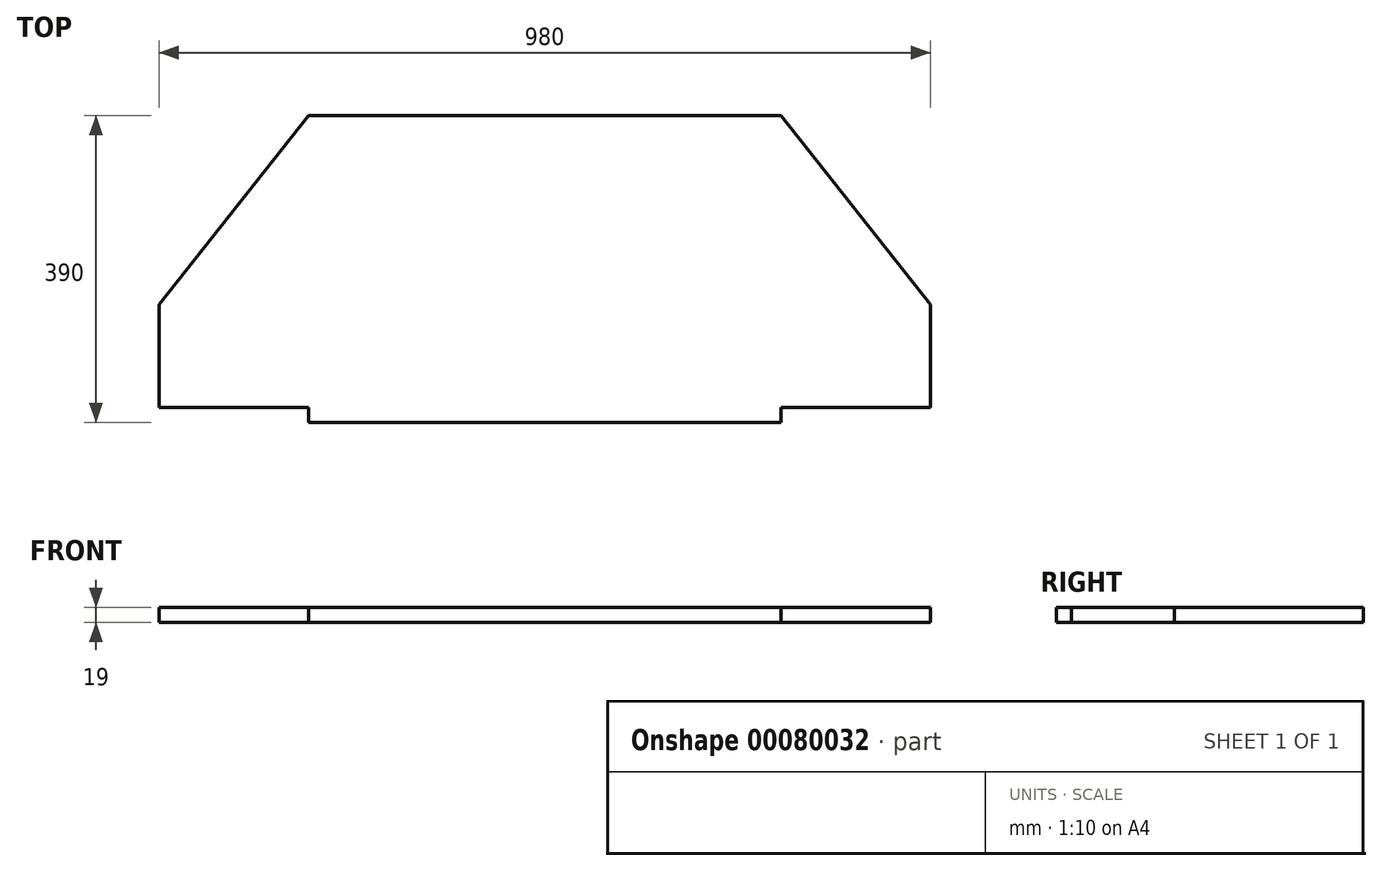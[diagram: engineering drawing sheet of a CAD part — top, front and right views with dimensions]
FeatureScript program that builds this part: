
annotation { "Feature Type Name" : "Feature", "Feature Type Description" : "" }
export const myFeature = defineFeature(function(context is Context, id is Id, definition is map)
    precondition{}
    {
        {
            var Q0;
            Q0=qCreatedBy(makeId("Top.planeOp"),FACE);
            var sketch = newSketch(context, id + "F0", { "sketchPlane" : qUnion([Q0])});
            skLineSegment(sketch, "E0.bottom", {"start": v(0, 0) * mm, "end": v(980, 0) * mm});
            skLineSegment(sketch, "E1.bottom", {"start": v(190, 390) * mm, "end": v(790, 390) * mm});
            skLineSegment(sketch, "E2", {"start": v(0, 0) * mm, "end": v(0, 150) * mm});
            skLineSegment(sketch, "E3", {"start": v(0, 150) * mm, "end": v(190, 390) * mm});
            skLineSegment(sketch, "E4", {"start": v(980, 0) * mm, "end": v(980, 150) * mm});
            skLineSegment(sketch, "E5", {"start": v(980, 150) * mm, "end": v(790, 390) * mm});
            skSolve(sketch);
        }
        {
            var Q0;
            Q0=makeQuery(id+"F0.imprint","IMPRINT",FACE,{"disambiguationData":[TD([[makeQuery(id+"F0.imprint","IMPRINT",EDGE,{"derivedFrom":sQuery(id+"F0.wireOp",EDGE,"E1.bottom")}),-1.0]])]});
            extrude(context, id + "F1", {"entities" : qUnion([Q0]), "depth" : 19 * mm});
        }
        {
            var Q0;
            Q0=makeQuery(id+"F1.opExtrude","CAP_FACE",FACE,{"disambiguationData":[OSD([sQuery(id+"F0.wireOp",EDGE,"E0.bottom"),sQuery(id+"F0.wireOp",EDGE,"E1.bottom"),sQuery(id+"F0.wireOp",EDGE,"gMk2omaf-fXzC-0NLB-TkjP-6ek92fSo4i94"),sQuery(id+"F0.wireOp",EDGE,"lLomHIAO-944t-a2IZ-Op6M-ri8957HSzVvk")])],"isStart":false});
            var sketch = newSketch(context, id + "F2", { "sketchPlane" : qUnion([Q0])});
            skLineSegment(sketch, "E6.bottom", {"start": v(190, 0) * mm, "end": v(0, 0) * mm});
            skLineSegment(sketch, "E6.top", {"start": v(190, 19) * mm, "end": v(0, 19) * mm});
            skLineSegment(sketch, "E6.left", {"start": v(190, 0) * mm, "end": v(190, 19) * mm});
            skLineSegment(sketch, "E6.right", {"start": v(0, 0) * mm, "end": v(0, 19) * mm});
            skSolve(sketch);
        }
        {
            var Q0;
            {var subQ0=sQuery(id+"F2.wireOp",EDGE,"E6.bottom");Q0=makeQuery(id+"F2.imprint","IMPRINT",FACE,{"disambiguationData":[TD([[makeQuery(id+"F2.imprint","IMPRINT",EDGE,{"derivedFrom":subQ0}),1.0]])]});}
            extrude(context, id + "F3", {"entities" : qUnion([Q0]), "operationType" : NewBodyOperationType.REMOVE, "oppositeDirection" : true, "depth" : 19 * mm});
        }
        {
            var Q0;
            Q0=makeQuery(id+"F1.opExtrude","CAP_FACE",FACE,{"disambiguationData":[OSD([sQuery(id+"F0.wireOp",EDGE,"E0.bottom"),sQuery(id+"F0.wireOp",EDGE,"E1.bottom"),sQuery(id+"F0.wireOp",EDGE,"gMk2omaf-fXzC-0NLB-TkjP-6ek92fSo4i94"),sQuery(id+"F0.wireOp",EDGE,"lLomHIAO-944t-a2IZ-Op6M-ri8957HSzVvk")])],"isStart":false});
            var sketch = newSketch(context, id + "F4", { "sketchPlane" : qUnion([Q0])});
            skLineSegment(sketch, "E7.bottom", {"start": v(980, 0) * mm, "end": v(790, 0) * mm});
            skLineSegment(sketch, "E7.top", {"start": v(980, 19) * mm, "end": v(790, 19) * mm});
            skLineSegment(sketch, "E7.left", {"start": v(980, 0) * mm, "end": v(980, 19) * mm});
            skLineSegment(sketch, "E7.right", {"start": v(790, 0) * mm, "end": v(790, 19) * mm});
            skSolve(sketch);
        }
        {
            var Q0;
            {var subQ0=sQuery(id+"F4.wireOp",EDGE,"E7.bottom");Q0=makeQuery(id+"F4.imprint","IMPRINT",FACE,{"disambiguationData":[TD([[makeQuery(id+"F4.imprint","IMPRINT",EDGE,{"derivedFrom":subQ0}),1.0]])]});}
            extrude(context, id + "F5", {"entities" : qUnion([Q0]), "operationType" : NewBodyOperationType.REMOVE, "oppositeDirection" : true, "depth" : 19 * mm});
        }
    });
